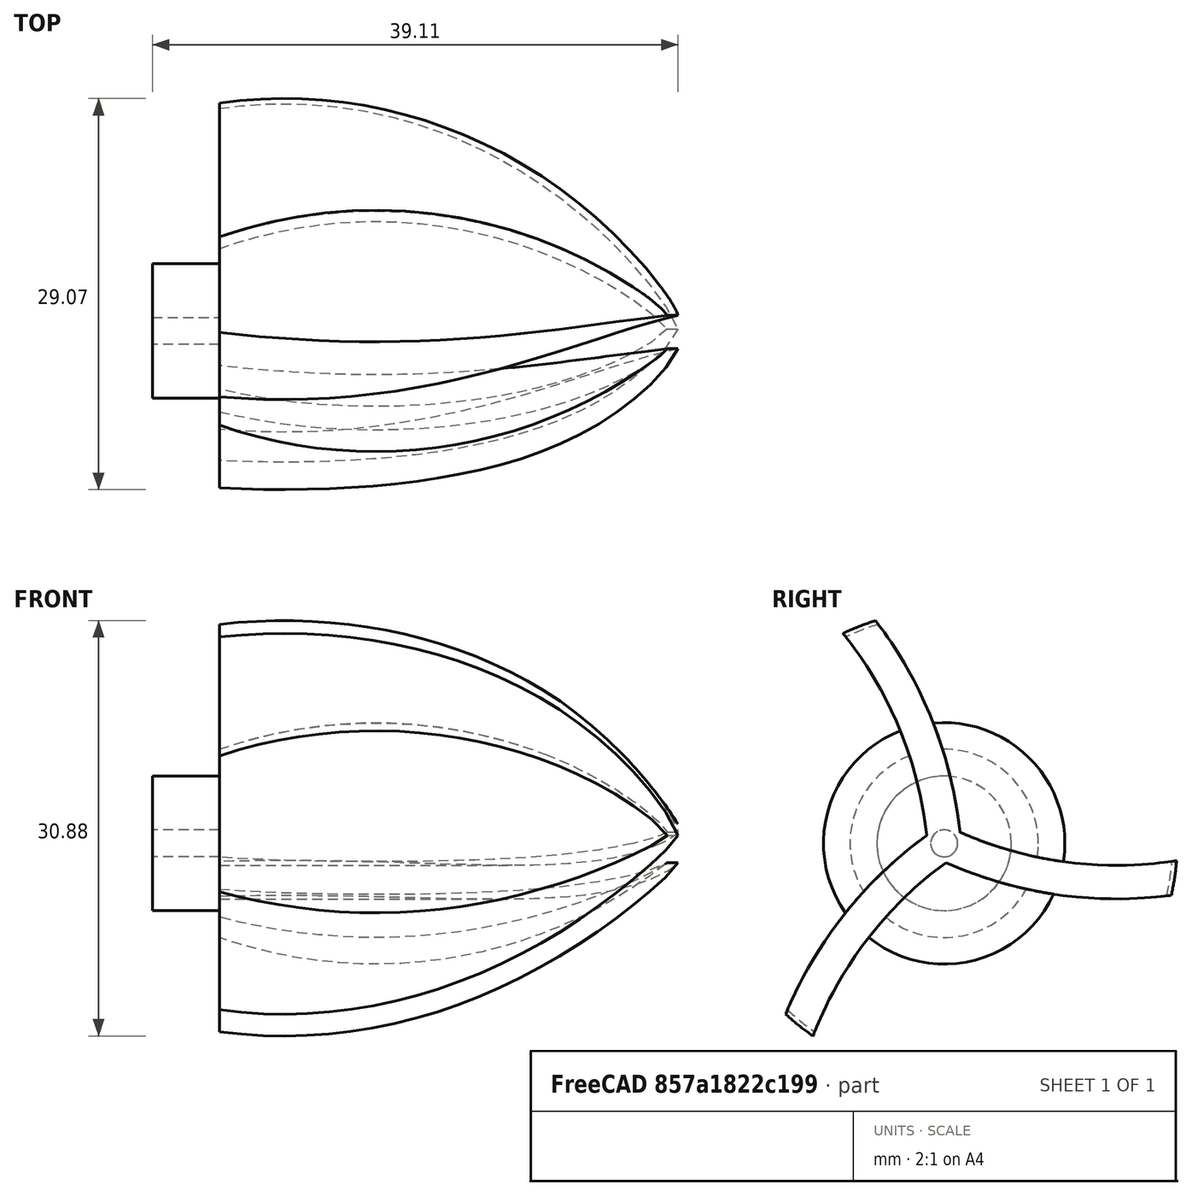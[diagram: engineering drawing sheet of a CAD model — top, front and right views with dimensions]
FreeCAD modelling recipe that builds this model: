
FCSTD DOCUMENT  (FreeCAD 0.18R4 (GitTag))
Label: Ariel Propeller Left
License: All rights reserved
LicenseURL: http://en.wikipedia.org/wiki/All_rights_reserved
objects: Sketcher::SketchObject×5, PartDesign::Revolution×1, PartDesign::AdditivePipe×1, PartDesign::PolarPattern×1, PartDesign::Groove×1, Part::Plane×1, PartDesign::Pad×1, PartDesign::Body×1, Mesh::Feature×1
note: 16 computed .brp shape members not serialized (recipe doc carries the construction recipe); baked Part::Feature solids carry a one-line shape summary decoded from their .brp

FEATURE [Sketcher::SketchObject] Sketch
  MapMode = 5
  Support = -> [XY_Plane]
  sketch-geometry (3):
    g0: LineSegment StartX=10 StartY=7 StartZ=0 EndX=10 EndY=0 EndZ=0
    g1: ArcOfCircle CenterX=21.5953 CenterY=-26.0235 CenterZ=0 NormalX=0 NormalY=0 NormalZ=1 AngleXU=0 Radius=35 StartAngle=0.83833 EndAngle=1.90847
    g2: LineSegment StartX=10 StartY=0 StartZ=0 EndX=45 EndY=-7.6525e-12 EndZ=0
  constraints (10):
    c: Vertical(g0)
    c: PointOnObject(g0,g-1)
    c: PointOnObject(g1,g-1)
    c: Radius(g1) = 35
    c: Coincident(g2,g0)
    c: Coincident(g2,g1)
    c: DistanceX(g-1,g0) = 10
    c: DistanceX(g-1,g1) = 45
    c: Coincident(g1,g0)
    c: DistanceY(g0,g0) = 7
FEATURE [PartDesign::Revolution] Revolution
  Angle = 360
  Axis = (1,0,0)
  Base = (0,0,0)
  Profile = -> Sketch
  ReferenceAxis = -> Sketch [H_Axis]
FEATURE [Sketcher::SketchObject] Sketch002
  MapMode = 5
  Support = -> [XY_Plane]
  sketch-geometry (6):
    g0: ArcOfCircle [constr] CenterX=21.5953 CenterY=26.0235 CenterZ=0 NormalX=0 NormalY=0 NormalZ=1 AngleXU=0 Radius=35 StartAngle=4.37471 EndAngle=5.44486
    g1: LineSegment [constr] StartX=10 StartY=7 StartZ=0 EndX=10 EndY=-7 EndZ=0
    g2: LineSegment StartX=10 StartY=1.25 StartZ=0 EndX=10 EndY=-1.25 EndZ=0
    g3: LineSegment StartX=10 StartY=1.25 StartZ=0 EndX=45 EndY=1.25 EndZ=0
    g4: LineSegment StartX=10 StartY=-1.25 StartZ=0 EndX=45 EndY=-1.25 EndZ=0
    g5: LineSegment StartX=45 StartY=1.25 StartZ=0 EndX=45 EndY=-1.25 EndZ=0
  constraints (13):
    c: Coincident(g1,g0)
    c: DistanceY(g1,g1) = 14
    c: PointOnObject(g2,g1)
    c: Symmetric(g2,g2,g-1)
    c: DistanceY(g2,g2) = 2.5
    c: Coincident(g3,g2)
    c: Coincident(g4,g2)
    c: Coincident(g5,g3)
    c: Coincident(g5,g4)
    c: DistanceY(g5,g5) = 2.5
    c: Horizontal(g3)
    c: PointOnObject(g0,g5)
    c: Vertical(g3,g4)
FEATURE [Sketcher::SketchObject] Sketch003
  ExternalGeometry = -> [Sketch002]
  MapMode = 5
  Placement = pos=(0,0,0) rot=(0.57735,0.57735,0.57735;2.0944rad)
  Support = -> [YZ_Plane]
  sketch-geometry (1):
    g0: ArcOfCircle CenterX=-29.8998 CenterY=-2.4499 CenterZ=0 NormalX=0 NormalY=0 NormalZ=1 AngleXU=0 Radius=30 StartAngle=0.0817544 EndAngle=0.845541
  constraints (4):
    c: DistanceX(g-1,g0) = -10
    c: DistanceY(g-1,g0) = 20
    c: Radius(g0) = 30
    c: Coincident(g0,g-1)
FEATURE [PartDesign::AdditivePipe] AdditivePipe
  AuxilleryCurvelinear = true
  AuxillerySpineTangent = false
  BaseFeature = -> Revolution
  Binormal = (0,0,0)
  Mode = 0
  Profile = -> Sketch002
  Spine = -> Sketch003
  SpineTangent = false
  Transformation = 0
  Transition = 0
FEATURE [PartDesign::PolarPattern] PolarPattern
  Angle = 360
  Axis = -> X_Axis
  BaseFeature = -> AdditivePipe
  Occurrences = 3
  Originals = -> [AdditivePipe]
FEATURE [Sketcher::SketchObject] Sketch004
  ExternalGeometry = -> [PolarPattern]
  MapMode = 5
  Support = -> [XY_Plane]
  sketch-geometry (3):
    g0: ArcOfCircle CenterX=14.7884 CenterY=-17.6709 CenterZ=0 NormalX=0 NormalY=0 NormalZ=1 AngleXU=0 Radius=35 StartAngle=0.529246 EndAngle=1.70804
    g1: ArcOfCircle CenterX=10.9237 CenterY=-7.98781 CenterZ=0 NormalX=0 NormalY=0 NormalZ=1 AngleXU=0 Radius=35 StartAngle=0.230252 EndAngle=1.59719
    g2: LineSegment StartX=10 StartY=27 StartZ=0 EndX=10 EndY=17 EndZ=0
FEATURE [PartDesign::Groove] Groove
  Angle = 360
  Axis = (1,0,0)
  Base = (0,0,0)
  BaseFeature = -> PolarPattern
  Profile = -> Sketch004
  ReferenceAxis = -> X_Axis
FEATURE [Part::Plane] Plane
  AttacherType = Attacher::AttachEngine3D
  Length = 10
  Placement = pos=(5,0,0) rot=(0.57735,0.57735,0.57735;2.0944rad)
  Width = 10
FEATURE [Sketcher::SketchObject] Sketch001
  MapMode = 5
  Placement = pos=(5,0,0) rot=(0.57735,0.57735,0.57735;2.0944rad)
  Support = -> [Plane]
  sketch-geometry (2):
    g0: Circle CenterX=0 CenterY=0 CenterZ=0 NormalX=0 NormalY=0 NormalZ=1 AngleXU=0 Radius=5
    g1: Circle CenterX=0 CenterY=0 CenterZ=0 NormalX=0 NormalY=0 NormalZ=1 AngleXU=0 Radius=1
  constraints (4):
    c: Radius(g0) = 5
    c: Coincident(g1,g0)
    c: Radius(g1) = 1
    c: Coincident(g0,g-1)
FEATURE [PartDesign::Pad] Pad
  BaseFeature = -> Groove
  Length = 10
  Length2 = 100
  Profile = -> Sketch001
  Type = 0
FEATURE [PartDesign::Body] Body
  Group = -> [Sketch,Revolution,Sketch001,Sketch002,Sketch003,AdditivePipe,PolarPattern,Sketch004,Groove,Pad]
  Origin = -> Origin
  Tip = -> Pad
FEATURE [Mesh::Feature] Mesh  label="Body (Meshed)"
